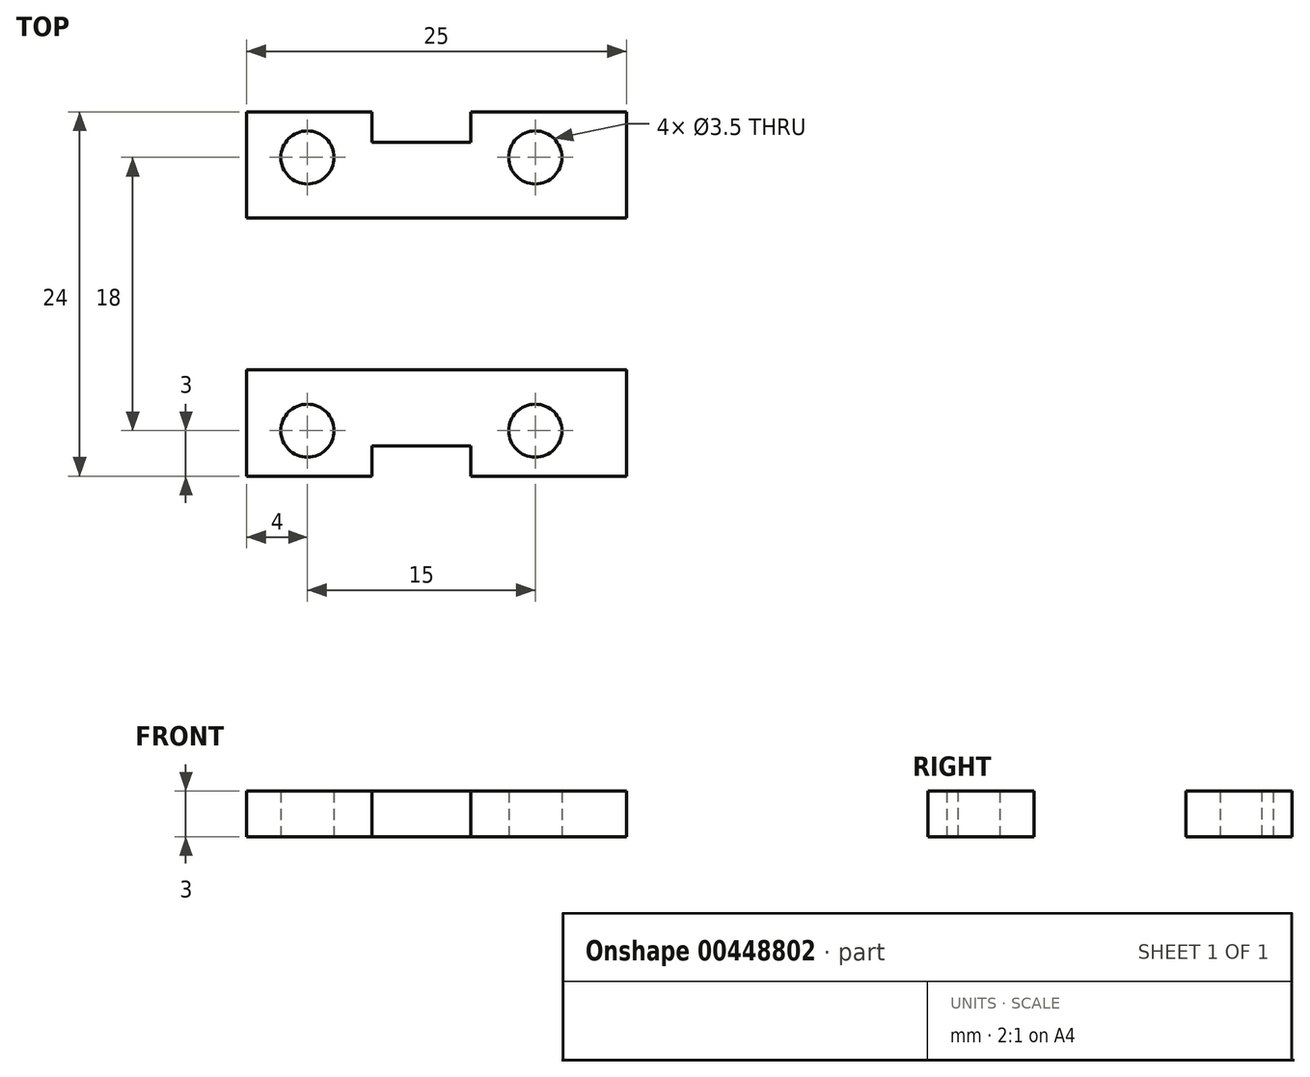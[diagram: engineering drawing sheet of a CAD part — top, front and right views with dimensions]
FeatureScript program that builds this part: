
annotation { "Feature Type Name" : "Feature", "Feature Type Description" : "" }
export const myFeature = defineFeature(function(context is Context, id is Id, definition is map)
    precondition{}
    {
        {
            var Q0;
            Q0=qCreatedBy(makeId("Top.planeOp"),FACE);
            var sketch = newSketch(context, id + "F0", { "sketchPlane" : qUnion([Q0])});
            skLineSegment(sketch, "E0.bottom", {"start": v(0, 0) * mm, "end": v(25, 0) * mm});
            skLineSegment(sketch, "E0.top", {"start": v(0, 7) * mm, "end": v(25, 7) * mm});
            skLineSegment(sketch, "E0.left", {"start": v(0, 0) * mm, "end": v(0, 7) * mm});
            skLineSegment(sketch, "E0.right", {"start": v(25, 0) * mm, "end": v(25, 7) * mm});
            skCircle(sketch, "E1", {"center": v(4, 4) * mm, "radius": 1.75 * mm});
            skCircle(sketch, "E2", {"center": v(19, 4) * mm, "radius": 1.75 * mm});
            skSolve(sketch);
        }
        {
            var Q0;
            Q0=qSketchRegion(id+"F0",true);
            extrude(context, id + "F1", {"entities" : qUnion([Q0]), "depth" : 3 * mm});
        }
        {
            var Q0;
            Q0=makeQuery(id+"F1.opExtrude","CAP_FACE",FACE,{"disambiguationData":[OSD([sQuery(id+"F0.wireOp",EDGE,"E0.bottom"),sQuery(id+"F0.wireOp",EDGE,"E0.top"),sQuery(id+"F0.wireOp",EDGE,"E0.left"),sQuery(id+"F0.wireOp",EDGE,"E0.right"),sQuery(id+"F0.wireOp",EDGE,"E1"),sQuery(id+"F0.wireOp",EDGE,"E2")])],"isStart":false});
            var sketch = newSketch(context, id + "F2", { "sketchPlane" : qUnion([Q0])});
            skLineSegment(sketch, "E3", {"start": v(4, 4) * mm, "end": v(19, 4) * mm, "construction": true});
            skLineSegment(sketch, "E4.bottom", {"start": v(8.25, 7) * mm, "end": v(14.75, 7) * mm});
            skLineSegment(sketch, "E4.top", {"start": v(8.25, 5) * mm, "end": v(14.75, 5) * mm});
            skLineSegment(sketch, "E4.left", {"start": v(8.25, 7) * mm, "end": v(8.25, 5) * mm});
            skLineSegment(sketch, "E4.right", {"start": v(14.75, 7) * mm, "end": v(14.75, 5) * mm});
            skPoint(sketch, "E5", {"position": v(11.5, 5) * mm});
            skPoint(sketch, "E6", {"position": v(11.5, 4) * mm});
            skSolve(sketch);
        }
        {
            var Q0;
            Q0=makeQuery(id+"F2.imprint","IMPRINT",FACE,{"disambiguationData":[TD([[makeQuery(id+"F2.imprint","IMPRINT",EDGE,{"derivedFrom":sQuery(id+"F2.wireOp",EDGE,"E4.bottom")}),-1.0]])]});
            extrude(context, id + "F3", {"entities" : qUnion([Q0]), "operationType" : NewBodyOperationType.REMOVE, "endBound" : BoundingType.THROUGH_ALL, "oppositeDirection" : true, "depth" : 25 * mm});
        }
        {
            var Q0;
            Q0=makeQuery(id+"F1.opExtrude","SWEPT_FACE",FACE,{"disambiguationData":[OSD([sQuery(id+"F0.wireOp",EDGE,"E0.bottom")])]});
            cPlane(context, id + "F4", {"entities" : qUnion([Q0]), "cplaneType" : CPlaneType.OFFSET, "offset" : 5 * mm, "width" : 150 * mm, "height" : 150 * mm});
        }
        {
            var Q0;
            Q0=makeQuery(id+"F1.opExtrude","SWEPT_BODY",BODY,{"disambiguationData":[OSD([sQuery(id+"F0.wireOp",EDGE,"E0.bottom"),sQuery(id+"F0.wireOp",EDGE,"E0.top"),sQuery(id+"F0.wireOp",EDGE,"E0.left"),sQuery(id+"F0.wireOp",EDGE,"E0.right"),sQuery(id+"F0.wireOp",EDGE,"E1"),sQuery(id+"F0.wireOp",EDGE,"E2")])]});
            var Q1;
            Q1=qCreatedBy(id+"F4.planeOp",FACE);
            mirror(context, id + "F5", {"entities" : qUnion([Q0]), "mirrorPlane" : qUnion([Q1])});
        }
    });
